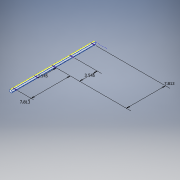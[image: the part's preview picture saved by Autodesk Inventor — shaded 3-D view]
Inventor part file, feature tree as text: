
AUTODESK INVENTOR PART (.ipt)
format: ipt  version: 2017 (Build 210142000, 142)  size: 148,480 bytes
history: native  units: in
note: dims shown in document units (in); Inventor stores cm internally (conversion verified against a paired STEP export)
features: sketch x5, split x1, fillet x1
ambient origin geometry x8: Origin, YZ Plane, XZ Plane, XY Plane, X Axis, Y Axis, Z Axis, Center Point
bodies: Solid1 (feature_tree)
feature tree (7):
  sketch  "Sketch1"  dims[d11=16.75in]
  split  "Split1"
  sketch  "Sketch3"  dims[d13=7.8125in]
  sketch  "Sketch4"  dims[d14=3.5453in]
  sketch  "Sketch5"  dims[d15=3.5453in]
  sketch  "Sketch2"  dims[d12=7.8125in]
  fillet  "Fillet1"  Radius=8.5in
